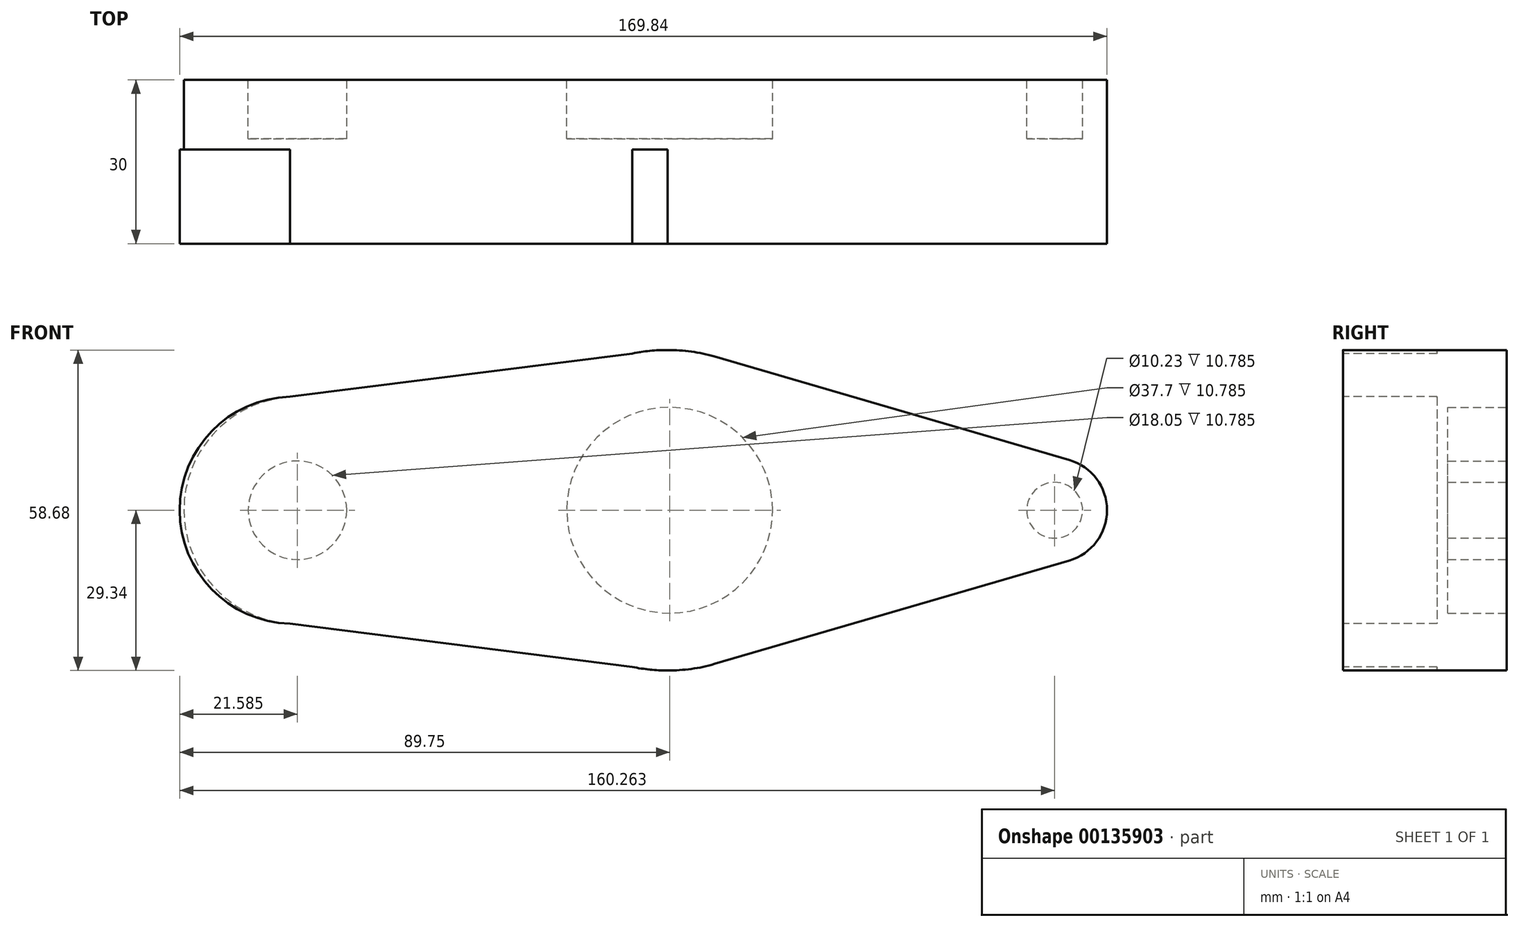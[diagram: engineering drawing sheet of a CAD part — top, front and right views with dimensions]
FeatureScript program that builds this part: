
annotation { "Feature Type Name" : "Feature", "Feature Type Description" : "" }
export const myFeature = defineFeature(function(context is Context, id is Id, definition is map)
    precondition{}
    {
        {
            var Q0;
            Q0=qCreatedBy(makeId("Front.planeOp"),FACE);
            var sketch = newSketch(context, id + "F0", { "sketchPlane" : qUnion([Q0])});
            skCircle(sketch, "E0", {"center": v(0, 0) * mm, "radius": 29.34 * mm});
            skCircle(sketch, "E1", {"center": v(70.51, 0) * mm, "radius": 9.58 * mm});
            skCircle(sketch, "E2", {"center": v(-68.16, 0) * mm, "radius": 20.8 * mm});
            skLineSegment(sketch, "E3", {"start": v(-3.68, -29.11) * mm, "end": v(-70.77, -20.64) * mm});
            skLineSegment(sketch, "E4", {"start": v(-70.77, 20.64) * mm, "end": v(-3.68, 29.11) * mm});
            skLineSegment(sketch, "E5", {"start": v(73.2, -9.2) * mm, "end": v(8.22, -28.17) * mm});
            skLineSegment(sketch, "E6", {"start": v(8.22, 28.17) * mm, "end": v(73.2, 9.2) * mm});
            skCircle(sketch, "E7", {"center": v(70.51, 0) * mm, "radius": 5.12 * mm});
            skCircle(sketch, "E8", {"center": v(0, 0) * mm, "radius": 18.85 * mm});
            skCircle(sketch, "E9", {"center": v(-68.16, 0) * mm, "radius": 9.02 * mm});
            skSolve(sketch);
        }
        {
            var Q0;
            {var subQ0=sQuery(id+"F0.wireOp",EDGE,"E5");Q0=makeQuery(id+"F0.imprint","IMPRINT",FACE,{"disambiguationData":[TD([[makeQuery(id+"F0.imprint","IMPRINT",EDGE,{"derivedFrom":subQ0}),-1.0]])]});}
            var Q1;
            Q1=makeQuery(id+"F0.imprint","IMPRINT",FACE,{"disambiguationData":[TD([[makeQuery(id+"F0.imprint","IMPRINT",EDGE,{"derivedFrom":sQuery(id+"F0.wireOp",EDGE,"E7")}),-1.0]])]});
            var Q2;
            Q2=makeQuery(id+"F0.imprint","IMPRINT",FACE,{"disambiguationData":[TD([[makeQuery(id+"F0.imprint","IMPRINT",EDGE,{"derivedFrom":sQuery(id+"F0.wireOp",EDGE,"E7")}),1.0]])]});
            var Q3;
            Q3=makeQuery(id+"F0.imprint","IMPRINT",FACE,{"disambiguationData":[TD([[makeQuery(id+"F0.imprint","IMPRINT",EDGE,{"derivedFrom":sQuery(id+"F0.wireOp",EDGE,"E8")}),-1.0]])]});
            var Q4;
            Q4=makeQuery(id+"F0.imprint","IMPRINT",FACE,{"disambiguationData":[TD([[makeQuery(id+"F0.imprint","IMPRINT",EDGE,{"derivedFrom":sQuery(id+"F0.wireOp",EDGE,"E8")}),1.0]])]});
            var Q5;
            {var subQ0=sQuery(id+"F0.wireOp",EDGE,"E3");Q5=makeQuery(id+"F0.imprint","IMPRINT",FACE,{"disambiguationData":[TD([[makeQuery(id+"F0.imprint","IMPRINT",EDGE,{"derivedFrom":subQ0}),-1.0]])]});}
            var Q6;
            Q6=makeQuery(id+"F0.imprint","IMPRINT",FACE,{"disambiguationData":[TD([[makeQuery(id+"F0.imprint","IMPRINT",EDGE,{"derivedFrom":sQuery(id+"F0.wireOp",EDGE,"E9")}),-1.0]])]});
            var Q7;
            Q7=makeQuery(id+"F0.imprint","IMPRINT",FACE,{"disambiguationData":[TD([[makeQuery(id+"F0.imprint","IMPRINT",EDGE,{"derivedFrom":sQuery(id+"F0.wireOp",EDGE,"E9")}),1.0]])]});
            extrude(context, id + "F1", {"entities" : qUnion([Q0, Q1, Q2, Q3, Q4, Q5, Q6, Q7]), "depth" : 30 * mm});
        }
        {
            var Q0;
            Q0=qCreatedBy(makeId("Front.planeOp"),FACE);
            cPlane(context, id + "F5", {"entities" : qUnion([Q0]), "cplaneType" : CPlaneType.OFFSET, "offset" : 30 * mm, "width" : 150 * mm, "height" : 150 * mm});
        }
        {
            var Q0;
            Q0=makeQuery(id+"F0.imprint","IMPRINT",FACE,{"disambiguationData":[TD([[makeQuery(id+"F0.imprint","IMPRINT",EDGE,{"derivedFrom":sQuery(id+"F0.wireOp",EDGE,"E9")}),1.0]])]});
            var Q1;
            Q1=makeQuery(id+"F0.imprint","IMPRINT",FACE,{"disambiguationData":[TD([[makeQuery(id+"F0.imprint","IMPRINT",EDGE,{"derivedFrom":sQuery(id+"F0.wireOp",EDGE,"E8")}),1.0]])]});
            var Q2;
            Q2=makeQuery(id+"F0.imprint","IMPRINT",FACE,{"disambiguationData":[TD([[makeQuery(id+"F0.imprint","IMPRINT",EDGE,{"derivedFrom":sQuery(id+"F0.wireOp",EDGE,"E7")}),1.0]])]});
            var Q3;
            Q3=sQuery(id+"F0.wireOp",EDGE,"E8");
            var Q4;
            Q4=sQuery(id+"F0.wireOp",EDGE,"E9");
            var Q5;
            Q5=sQuery(id+"F0.wireOp",EDGE,"E7");
            extrude(context, id + "F6", {"entities" : qUnion([Q0, Q1, Q2]), "operationType" : NewBodyOperationType.REMOVE, "surfaceEntities" : qUnion([Q3, Q4, Q5]), "depth" : 10.79 * mm});
        }
        {
            var Q0;
            Q0=qCreatedBy(id+"F5.planeOp",FACE);
            var sketch = newSketch(context, id + "F2", { "sketchPlane" : qUnion([Q0])});
            skCircle(sketch, "E10", {"center": v(-0.78, 0) * mm, "radius": 29.34 * mm});
            skCircle(sketch, "E11", {"center": v(69.73, 0) * mm, "radius": 9.58 * mm});
            skCircle(sketch, "E12", {"center": v(-68.95, 0) * mm, "radius": 20.8 * mm});
            skSolve(sketch);
        }
        {
            var Q0;
            Q0=makeQuery(id+"F2.imprint","IMPRINT",FACE,{"disambiguationData":[TD([[makeQuery(id+"F2.imprint","IMPRINT",EDGE,{"derivedFrom":sQuery(id+"F2.wireOp",EDGE,"E12")}),1.0]])]});
            var Q1;
            Q1=makeQuery(id+"F2.imprint","IMPRINT",FACE,{"disambiguationData":[TD([[makeQuery(id+"F2.imprint","IMPRINT",EDGE,{"derivedFrom":sQuery(id+"F2.wireOp",EDGE,"E10")}),1.0]])]});
            var Q2;
            Q2=makeQuery(id+"F2.imprint","IMPRINT",FACE,{"disambiguationData":[TD([[makeQuery(id+"F2.imprint","IMPRINT",EDGE,{"derivedFrom":sQuery(id+"F2.wireOp",EDGE,"E11")}),1.0]])]});
            var Q3;
            Q3=sQuery(id+"F2.wireOp",EDGE,"E10");
            var Q4;
            Q4=sQuery(id+"F2.wireOp",EDGE,"E12");
            var Q5;
            Q5=sQuery(id+"F2.wireOp",EDGE,"E11");
            extrude(context, id + "F3", {"entities" : qUnion([Q0, Q1, Q2]), "operationType" : NewBodyOperationType.ADD, "surfaceEntities" : qUnion([Q3, Q4, Q5]), "oppositeDirection" : true, "depth" : 17.25 * mm});
        }
        {
            var Q0;
            Q0=makeQuery(id+"F0.imprint","IMPRINT",FACE,{"disambiguationData":[TD([[makeQuery(id+"F0.imprint","IMPRINT",EDGE,{"derivedFrom":sQuery(id+"F0.wireOp",EDGE,"E9")}),-1.0]])]});
            var Q1;
            Q1=makeQuery(id+"F0.imprint","IMPRINT",FACE,{"disambiguationData":[TD([[makeQuery(id+"F0.imprint","IMPRINT",EDGE,{"derivedFrom":sQuery(id+"F0.wireOp",EDGE,"E8")}),-1.0]])]});
            var Q2;
            Q2=makeQuery(id+"F0.imprint","IMPRINT",FACE,{"disambiguationData":[TD([[makeQuery(id+"F0.imprint","IMPRINT",EDGE,{"derivedFrom":sQuery(id+"F0.wireOp",EDGE,"E7")}),-1.0]])]});
            extrude(context, id + "F4", {"entities" : qUnion([Q0, Q1, Q2]), "operationType" : NewBodyOperationType.REMOVE, "oppositeDirection" : true, "depth" : 0.93 * mm});
        }
    });
